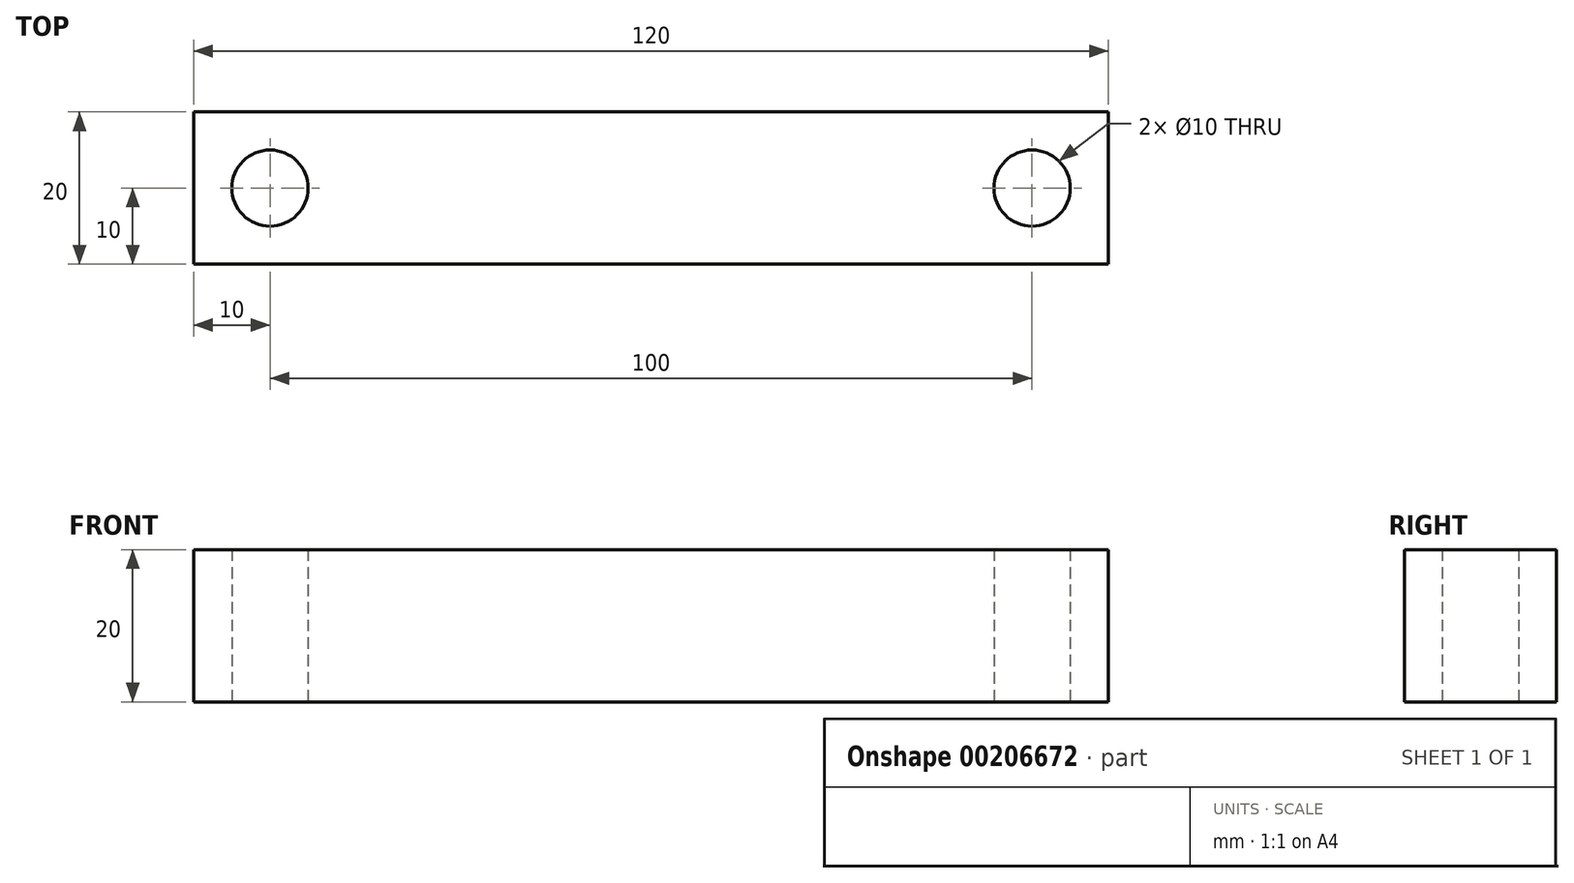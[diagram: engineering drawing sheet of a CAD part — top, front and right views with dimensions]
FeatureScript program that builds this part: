
annotation { "Feature Type Name" : "Feature", "Feature Type Description" : "" }
export const myFeature = defineFeature(function(context is Context, id is Id, definition is map)
    precondition{}
    {
        {
            var Q0;
            Q0=qCreatedBy(makeId("Top.planeOp"),FACE);
            var sketch = newSketch(context, id + "F0", { "sketchPlane" : qUnion([Q0])});
            skCircle(sketch, "E0", {"center": v(0, 0) * mm, "radius": 5 * mm});
            skCircle(sketch, "E1", {"center": v(100, 0) * mm, "radius": 5 * mm});
            skLineSegment(sketch, "E2.bottom", {"start": v(-10, 10) * mm, "end": v(110, 10) * mm});
            skLineSegment(sketch, "E2.top", {"start": v(-10, -10) * mm, "end": v(110, -10) * mm});
            skLineSegment(sketch, "E2.left", {"start": v(-10, 10) * mm, "end": v(-10, -10) * mm});
            skLineSegment(sketch, "E2.right", {"start": v(110, 10) * mm, "end": v(110, -10) * mm});
            skSolve(sketch);
        }
        {
            var Q0;
            Q0=makeQuery(id+"F0.imprint","IMPRINT",FACE,{"disambiguationData":[TD([[makeQuery(id+"F0.imprint","IMPRINT",EDGE,{"derivedFrom":sQuery(id+"F0.wireOp",EDGE,"E0")}),-1.0]])]});
            extrude(context, id + "F1", {"entities" : qUnion([Q0]), "depth" : 20 * mm});
        }
    });
